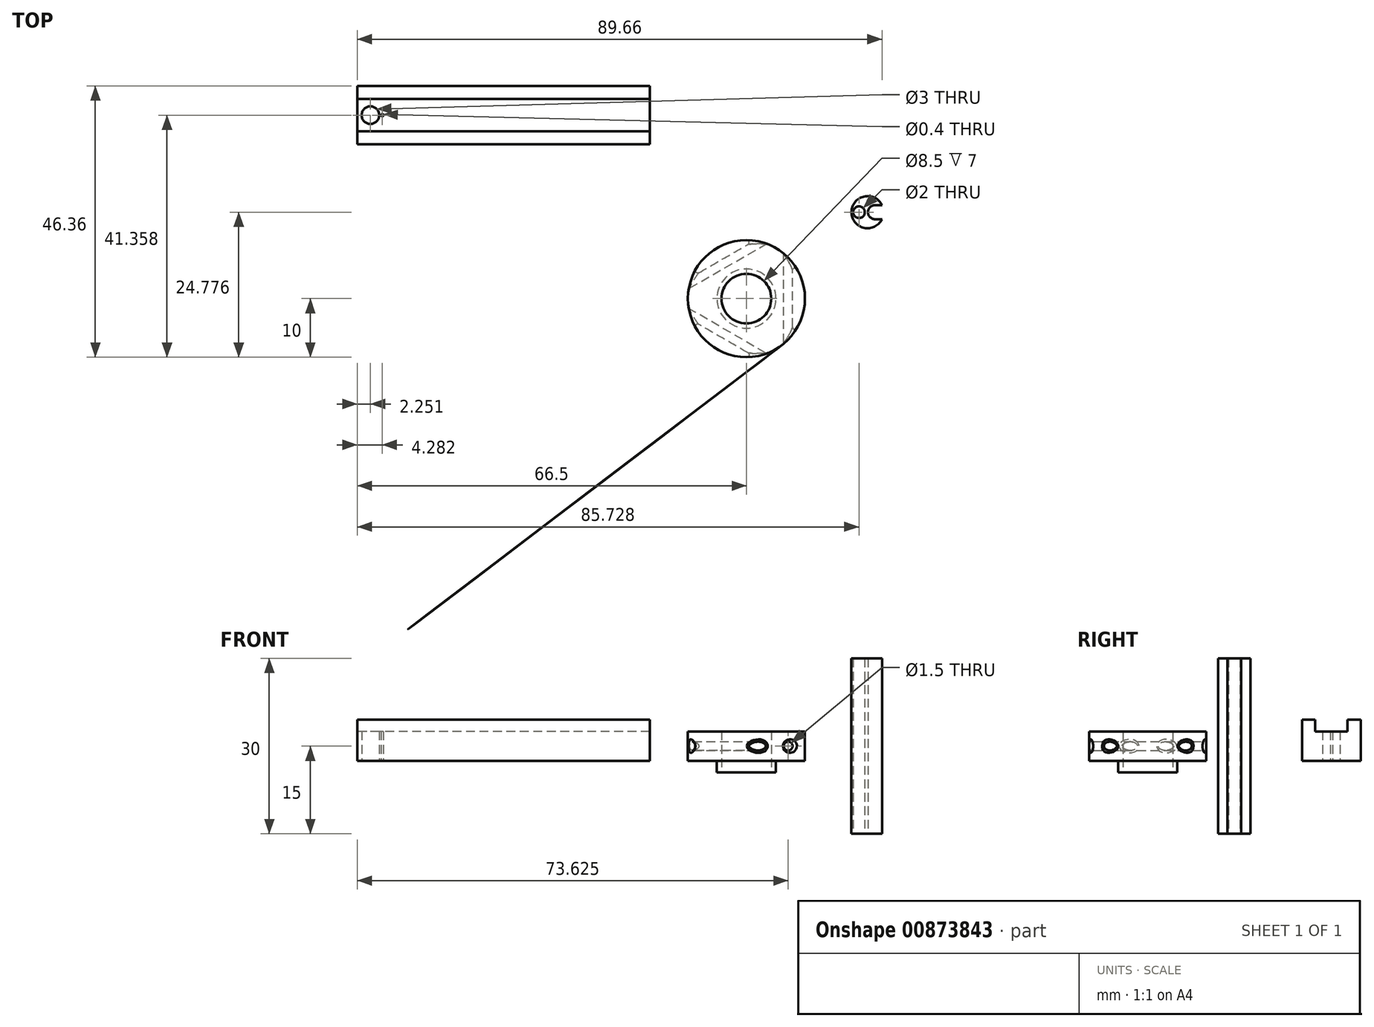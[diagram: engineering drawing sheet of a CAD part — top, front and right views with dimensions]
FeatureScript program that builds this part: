
annotation { "Feature Type Name" : "Feature", "Feature Type Description" : "" }
export const myFeature = defineFeature(function(context is Context, id is Id, definition is map)
    precondition{}
    {
        {
            var Q0;
            Q0=qCreatedBy(makeId("Top.planeOp"),FACE);
            var sketch = newSketch(context, id + "F0", { "sketchPlane" : qUnion([Q0])});
            skCircle(sketch, "E0", {"center": v(0, 0) * mm, "radius": 10 * mm});
            skCircle(sketch, "E1", {"center": v(0, 0) * mm, "radius": 5.05 * mm});
            skCircle(sketch, "E2", {"center": v(0, 0) * mm, "radius": 4.25 * mm});
            skSolve(sketch);
        }
        {
            var Q0;
            Q0=makeQuery(id+"F0.imprint","IMPRINT",FACE,{"disambiguationData":[TD([[makeQuery(id+"F0.imprint","IMPRINT",EDGE,{"derivedFrom":sQuery(id+"F0.wireOp",EDGE,"E0")}),1.0]])]});
            extrude(context, id + "F1", {"entities" : qUnion([Q0]), "depth" : 5 * mm, "offsetDistance" : 25 * mm});
        }
        {
            var Q0;
            Q0=makeQuery(id+"F0.imprint","IMPRINT",FACE,{"disambiguationData":[TD([[makeQuery(id+"F0.imprint","IMPRINT",EDGE,{"derivedFrom":sQuery(id+"F0.wireOp",EDGE,"E1")}),1.0]])]});
            extrude(context, id + "F2", {"entities" : qUnion([Q0]), "operationType" : NewBodyOperationType.ADD, "depth" : 5 * mm, "offsetDistance" : 25 * mm});
        }
        {
            var Q0;
            Q0=makeQuery(id+"F0.imprint","IMPRINT",FACE,{"disambiguationData":[TD([[makeQuery(id+"F0.imprint","IMPRINT",EDGE,{"derivedFrom":sQuery(id+"F0.wireOp",EDGE,"E1")}),1.0]])]});
            extrude(context, id + "F3", {"entities" : qUnion([Q0]), "operationType" : NewBodyOperationType.ADD, "oppositeDirection" : true, "depth" : 2 * mm, "offsetDistance" : 25 * mm});
        }
        {
            var Q0;
            Q0=qCreatedBy(makeId("Top.planeOp"),FACE);
            cPlane(context, id + "F4", {"entities" : qUnion([Q0]), "cplaneType" : CPlaneType.OFFSET, "offset" : 2.5 * mm, "width" : 150 * mm, "height" : 150 * mm});
        }
        {
            var Q0;
            Q0=qCreatedBy(id+"F4.planeOp",FACE);
            var sketch = newSketch(context, id + "F5", { "sketchPlane" : qUnion([Q0])});
            skLineSegment(sketch, "E3.bottom", {"start": v(7.88, -12.5) * mm, "end": v(7.13, -12.5) * mm});
            skLineSegment(sketch, "E3.top", {"start": v(7.87, 12.5) * mm, "end": v(7.12, 12.5) * mm});
            skLineSegment(sketch, "E3.left", {"start": v(7.88, -12.5) * mm, "end": v(7.87, 12.5) * mm});
            skLineSegment(sketch, "E3.right", {"start": v(7.13, -12.5) * mm, "end": v(7.12, 12.5) * mm});
            skPoint(sketch, "E3.middle", {"position": v(7.5, 0) * mm});
            skLineSegment(sketch, "E4", {"start": v(7.12, 15.05) * mm, "end": v(7.13, -13.65) * mm});
            skLineSegment(sketch, "E5", {"start": v(4.25, 0) * mm, "end": v(10, 0) * mm});
            skPoint(sketch, "E6", {"position": v(7.12, 0) * mm});
            skLineSegment(sketch, "E7.1.0", {"start": v(6.87, -13.08) * mm, "end": v(7.24, -12.43) * mm});
            skLineSegment(sketch, "E7.1.1", {"start": v(-14.78, -0.58) * mm, "end": v(-14.4, 0.07) * mm});
            skLineSegment(sketch, "E7.1.2", {"start": v(9.45, -13.7) * mm, "end": v(-15.4, 0.65) * mm});
            skLineSegment(sketch, "E7.1.3", {"start": v(-14.78, -0.58) * mm, "end": v(6.87, -13.08) * mm});
            skLineSegment(sketch, "E7.2.0", {"start": v(-14.78, 0.58) * mm, "end": v(-14.4, -0.07) * mm});
            skLineSegment(sketch, "E7.2.1", {"start": v(6.87, 13.08) * mm, "end": v(7.24, 12.43) * mm});
            skLineSegment(sketch, "E7.2.2", {"start": v(-16.61, -1.34) * mm, "end": v(8.24, 13) * mm});
            skLineSegment(sketch, "E7.2.3", {"start": v(6.87, 13.08) * mm, "end": v(-14.78, 0.58) * mm});
            skPoint(sketch, "E7.center", {"position": v(-0.01, 0) * mm});
            skLineSegment(sketch, "E7.anchor1", {"start": v(-0.01, 0) * mm, "end": v(7.13, -13.65) * mm, "construction": true});
            skLineSegment(sketch, "E7.anchor2", {"start": v(-0.01, 0) * mm, "end": v(8.24, 13) * mm, "construction": true});
            skSolve(sketch);
        }
        {
            var Q0;
            {var subQ1=sQuery(id+"F5.wireOp",EDGE,"E3.left");var subQ7=sQuery(id+"F5.wireOp",EDGE,"E3.bottom");var subQ8=makeQuery(id+"F5.imprint","INTERSECT",VERTEX,{"derivedFrom":[subQ7,subQ1]});Q0=makeQuery(id+"F5.imprint","IMPRINT",FACE,{"disambiguationData":[TD([[makeQuery(id+"F5.imprint","IMPRINT",EDGE,{"disambiguationData":[TD([[subQ8,-1.0]])],"derivedFrom":subQ7}),-1.0]])]});}
            var Q1;
            {var subQ1=sQuery(id+"F5.wireOp",EDGE,"E3.left");var subQ5=sQuery(id+"F5.wireOp",EDGE,"E3.top");var subQ6=makeQuery(id+"F5.imprint","INTERSECT",VERTEX,{"derivedFrom":[subQ5,subQ1]});Q1=makeQuery(id+"F5.imprint","IMPRINT",FACE,{"disambiguationData":[TD([[makeQuery(id+"F5.imprint","IMPRINT",EDGE,{"disambiguationData":[TD([[subQ6,-1.0]])],"derivedFrom":subQ5}),1.0]])]});}
            var Q2;
            Q2=sQuery(id+"F5.wireOp",EDGE,"E3.right");
            revolve(context, id + "F6", {"operationType" : NewBodyOperationType.REMOVE, "surfaceOperationType" : NewSurfaceOperationType.NEW, "entities" : qUnion([Q0, Q1]), "axis" : qUnion([Q2]), "revolveType" : RevolveType.FULL, "oppositeDirection" : true});
        }
        {
            var Q0;
            {var subQ11=sQuery(id+"F5.wireOp",EDGE,"E7.2.3");Q0=makeQuery(id+"F5.imprint","IMPRINT",FACE,{"disambiguationData":[TD([[makeQuery(id+"F5.imprint","IMPRINT",EDGE,{"derivedFrom":subQ11}),1.0]])]});}
            var Q1;
            Q1=sQuery(id+"F5.wireOp",EDGE,"E7.2.2");
            revolve(context, id + "F7", {"operationType" : NewBodyOperationType.REMOVE, "surfaceOperationType" : NewSurfaceOperationType.NEW, "entities" : qUnion([Q0]), "axis" : qUnion([Q1]), "revolveType" : RevolveType.FULL, "oppositeDirection" : true});
        }
        {
            var Q0;
            {var subQ0=sQuery(id+"F5.wireOp",EDGE,"E7.1.3");Q0=makeQuery(id+"F5.imprint","IMPRINT",FACE,{"disambiguationData":[TD([[makeQuery(id+"F5.imprint","IMPRINT",EDGE,{"derivedFrom":subQ0}),1.0]])]});}
            var Q1;
            Q1=sQuery(id+"F5.wireOp",EDGE,"E7.1.2");
            revolve(context, id + "F8", {"operationType" : NewBodyOperationType.REMOVE, "surfaceOperationType" : NewSurfaceOperationType.NEW, "entities" : qUnion([Q0]), "axis" : qUnion([Q1]), "revolveType" : RevolveType.FULL, "oppositeDirection" : true});
        }
        {
            var Q0;
            Q0=makeQuery(id+"F7.boolean.opBoolean","INTERSECT",EDGE,{"disambiguationData":[OD(0.0)],"derivedFrom":[makeQuery(id+"F1.opExtrude","SWEPT_FACE",FACE,{"disambiguationData":[OSD([sQuery(id+"F0.wireOp",EDGE,"E0")])]}),makeQuery(id+"F7.opRevolve","SWEPT_FACE",FACE,{"disambiguationData":[OSD([sQuery(id+"F5.wireOp",EDGE,"E7.2.3")])]})]});
            var Q1;
            Q1=makeQuery(id+"F6.boolean.opBoolean","INTERSECT",EDGE,{"disambiguationData":[OD(1.0)],"derivedFrom":[makeQuery(id+"F1.opExtrude","SWEPT_FACE",FACE,{"disambiguationData":[OSD([sQuery(id+"F0.wireOp",EDGE,"E0")])]}),makeQuery(id+"F6.opRevolve","SWEPT_FACE",FACE,{"disambiguationData":[OSD([sQuery(id+"F5.wireOp",EDGE,"E3.left")])]})]});
            var Q2;
            Q2=makeQuery(id+"F8.boolean.opBoolean","INTERSECT",EDGE,{"disambiguationData":[OD(0.0)],"derivedFrom":[makeQuery(id+"F1.opExtrude","SWEPT_FACE",FACE,{"disambiguationData":[OSD([sQuery(id+"F0.wireOp",EDGE,"E0")])]}),makeQuery(id+"F8.opRevolve","SWEPT_FACE",FACE,{"disambiguationData":[OSD([sQuery(id+"F5.wireOp",EDGE,"E7.1.3")])]})]});
            var Q3;
            Q3=makeQuery(id+"F8.boolean.opBoolean","INTERSECT",EDGE,{"disambiguationData":[OD(1.0)],"derivedFrom":[makeQuery(id+"F1.opExtrude","SWEPT_FACE",FACE,{"disambiguationData":[OSD([sQuery(id+"F0.wireOp",EDGE,"E0")])]}),makeQuery(id+"F8.opRevolve","SWEPT_FACE",FACE,{"disambiguationData":[OSD([sQuery(id+"F5.wireOp",EDGE,"E7.1.3")])]})]});
            var Q4;
            Q4=makeQuery(id+"F6.boolean.opBoolean","INTERSECT",EDGE,{"disambiguationData":[OD(0.0)],"derivedFrom":[makeQuery(id+"F1.opExtrude","SWEPT_FACE",FACE,{"disambiguationData":[OSD([sQuery(id+"F0.wireOp",EDGE,"E0")])]}),makeQuery(id+"F6.opRevolve","SWEPT_FACE",FACE,{"disambiguationData":[OSD([sQuery(id+"F5.wireOp",EDGE,"E3.left")])]})]});
            var Q5;
            Q5=makeQuery(id+"F7.boolean.opBoolean","INTERSECT",EDGE,{"disambiguationData":[OD(1.0)],"derivedFrom":[makeQuery(id+"F1.opExtrude","SWEPT_FACE",FACE,{"disambiguationData":[OSD([sQuery(id+"F0.wireOp",EDGE,"E0")])]}),makeQuery(id+"F7.opRevolve","SWEPT_FACE",FACE,{"disambiguationData":[OSD([sQuery(id+"F5.wireOp",EDGE,"E7.2.3")])]})]});
            fillet(context, id + "F9", {"entities" : qUnion([Q0, Q1, Q2, Q3, Q4, Q5]), "radius" : 0.4 * mm, "tangentPropagation" : true, "allowEdgeOverflow" : false});
        }
        {
            var Q0;
            Q0=qCreatedBy(makeId("Top.planeOp"),FACE);
            var sketch = newSketch(context, id + "F10", { "sketchPlane" : qUnion([Q0])});
            skLineSegment(sketch, "E8.bottom", {"start": v(-16.5, 26.36) * mm, "end": v(-66.5, 26.36) * mm});
            skLineSegment(sketch, "E8.top", {"start": v(-16.5, 36.36) * mm, "end": v(-66.5, 36.36) * mm});
            skLineSegment(sketch, "E8.left", {"start": v(-16.5, 26.36) * mm, "end": v(-16.5, 36.36) * mm});
            skLineSegment(sketch, "E8.right", {"start": v(-66.5, 26.36) * mm, "end": v(-66.5, 36.36) * mm});
            skPoint(sketch, "E8.middle", {"position": v(-41.5, 31.36) * mm});
            skLineSegment(sketch, "E9.bottom", {"start": v(-16.5, 28.6) * mm, "end": v(-66.5, 28.6) * mm});
            skLineSegment(sketch, "E9.top", {"start": v(-16.5, 34.1) * mm, "end": v(-66.5, 34.1) * mm});
            skLineSegment(sketch, "E9.left", {"start": v(-16.5, 28.6) * mm, "end": v(-16.5, 34.1) * mm});
            skLineSegment(sketch, "E9.right", {"start": v(-66.5, 28.6) * mm, "end": v(-66.5, 34.1) * mm});
            skCircle(sketch, "E10", {"center": v(-64.25, 31.36) * mm, "radius": 1.5 * mm});
            skCircle(sketch, "E11", {"center": v(-62.22, 31.36) * mm, "radius": 0.2 * mm});
            skSolve(sketch);
        }
        {
            var Q0;
            {var subQ0=sQuery(id+"F10.wireOp",EDGE,"E8.bottom");Q0=makeQuery(id+"F10.imprint","IMPRINT",FACE,{"disambiguationData":[TD([[makeQuery(id+"F10.imprint","IMPRINT",EDGE,{"derivedFrom":subQ0}),-1.0]])]});}
            var Q1;
            {var subQ0=sQuery(id+"F10.wireOp",EDGE,"E8.top");Q1=makeQuery(id+"F10.imprint","IMPRINT",FACE,{"disambiguationData":[TD([[makeQuery(id+"F10.imprint","IMPRINT",EDGE,{"derivedFrom":subQ0}),1.0]])]});}
            extrude(context, id + "F11", {"entities" : qUnion([Q0, Q1]), "depth" : 7 * mm, "offsetDistance" : 25 * mm});
        }
        {
            var Q0;
            Q0 = qSketchRegion(id + "F10", true);
            extrude(context, id + "F12", {"entities" : qUnion([Q0]), "operationType" : NewBodyOperationType.ADD, "depth" : 5 * mm, "offsetDistance" : 25 * mm});
        }
        {
            var Q0;
            Q0=makeQuery(id+"F10.imprint","IMPRINT",FACE,{"disambiguationData":[TD([[makeQuery(id+"F10.imprint","IMPRINT",EDGE,{"derivedFrom":sQuery(id+"F10.wireOp",EDGE,"E10")}),1.0]])]});
            var Q1;
            Q1=makeQuery(id+"F10.imprint","IMPRINT",FACE,{"disambiguationData":[TD([[makeQuery(id+"F10.imprint","IMPRINT",EDGE,{"derivedFrom":sQuery(id+"F10.wireOp",EDGE,"E11")}),1.0]])]});
            extrude(context, id + "F13", {"entities" : qUnion([Q0, Q1]), "operationType" : NewBodyOperationType.REMOVE, "oppositeDirection" : true, "depth" : -5 * mm, "offsetDistance" : 25 * mm});
        }
        {
            var Q0;
            Q0=qCreatedBy(id+"F4.planeOp",FACE);
            var sketch = newSketch(context, id + "F14", { "sketchPlane" : qUnion([Q0])});
            skArc(sketch, "E12", {"start": v(23.16, 15.97) * mm, "mid": v(17.94, 14.78) * mm, "end": v(23.16, 13.57) * mm});
            skLineSegment(sketch, "E13.bottom", {"start": v(20.76, 15.97) * mm, "end": v(23.16, 15.97) * mm});
            skLineSegment(sketch, "E13.top", {"start": v(20.76, 13.57) * mm, "end": v(23.16, 13.57) * mm});
            skLineSegment(sketch, "E13.left", {"start": v(20.76, 15.97) * mm, "end": v(20.76, 13.57) * mm});
            skPoint(sketch, "E13.middle", {"position": v(23.44, 14.78) * mm});
            skCircle(sketch, "E14", {"center": v(19.23, 14.78) * mm, "radius": 1 * mm});
            skSolve(sketch);
        }
        {
            var Q0;
            Q0=makeQuery(id+"F14.imprint","IMPRINT",FACE,{"disambiguationData":[TD([[makeQuery(id+"F14.imprint","IMPRINT",EDGE,{"derivedFrom":sQuery(id+"F14.wireOp",EDGE,"E12")}),1.0]])]});
            extrude(context, id + "F15", {"entities" : qUnion([Q0]), "depth" : 30 * mm, "offsetDistance" : 25 * mm, "symmetric" : true});
        }
        {
            var Q0;
            Q0=makeQuery(id+"F15.opExtrude","SWEPT_EDGE",EDGE,{"disambiguationData":[OSD([sQuery(id+"F14.wireOp",EDGE,"E13.bottom"),sQuery(id+"F14.wireOp",EDGE,"E13.left")])]});
            var Q1;
            Q1=makeQuery(id+"F15.opExtrude","SWEPT_EDGE",EDGE,{"disambiguationData":[OSD([sQuery(id+"F14.wireOp",EDGE,"E13.top"),sQuery(id+"F14.wireOp",EDGE,"E13.left")])]});
            fillet(context, id + "F16", {"entities" : qUnion([Q0, Q1]), "radius" : 1.2 * mm, "tangentPropagation" : true, "allowEdgeOverflow" : false});
        }
    });
